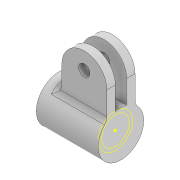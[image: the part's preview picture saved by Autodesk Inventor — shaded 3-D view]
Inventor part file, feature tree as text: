
AUTODESK INVENTOR PART (.ipt)
format: ipt  version: 2022 (Build 260153000, 153)  size: 179,712 bytes
history: native  units: mm
features: sketch x5, extrude x4, projected_geometry x2, fillet x1
ambient origin geometry x8: Origin, YZ Plane, XZ Plane, XY Plane, X Axis, Y Axis, Z Axis, Center Point
bodies: Solid1 (feature_tree)
feature tree (12):
  extrude  "Extrusion1"  Depth=12.2mm
  extrude  "Extrusion2"  Depth=20.0mm TaperAngle=0.0deg
  sketch  "Sketch5"  dims[d5=2.0mm d6=0.0mm d23=16.0mm]
  sketch  "Sketch6"  dims[d24=2.0mm d25=2.0mm d26=3.0mm]
  extrude  "Extrusion5"  Depth=16.0mm
  extrude  "Extrusion6"  Depth=3.0mm
  fillet  "Fillet2"  Radius=3.0mm
  sketch  "Sketch1"  dims[d0=9.8mm d1=12.2mm]
  sketch  "Sketch2"  dims[d2=2.0mm d3=20.0mm d4=0.0mm]
  projected_geometry  "Projected Loop1"
  projected_geometry  "Projected Loop2"
  sketch  "Sketch7"  dims[d27=3.0mm d28=24.0mm d29=0.0mm d30=4.0mm d31=6.0mm d32=8.0mm d33=100.0mm d34=0.0mm d35=3.0mm]
